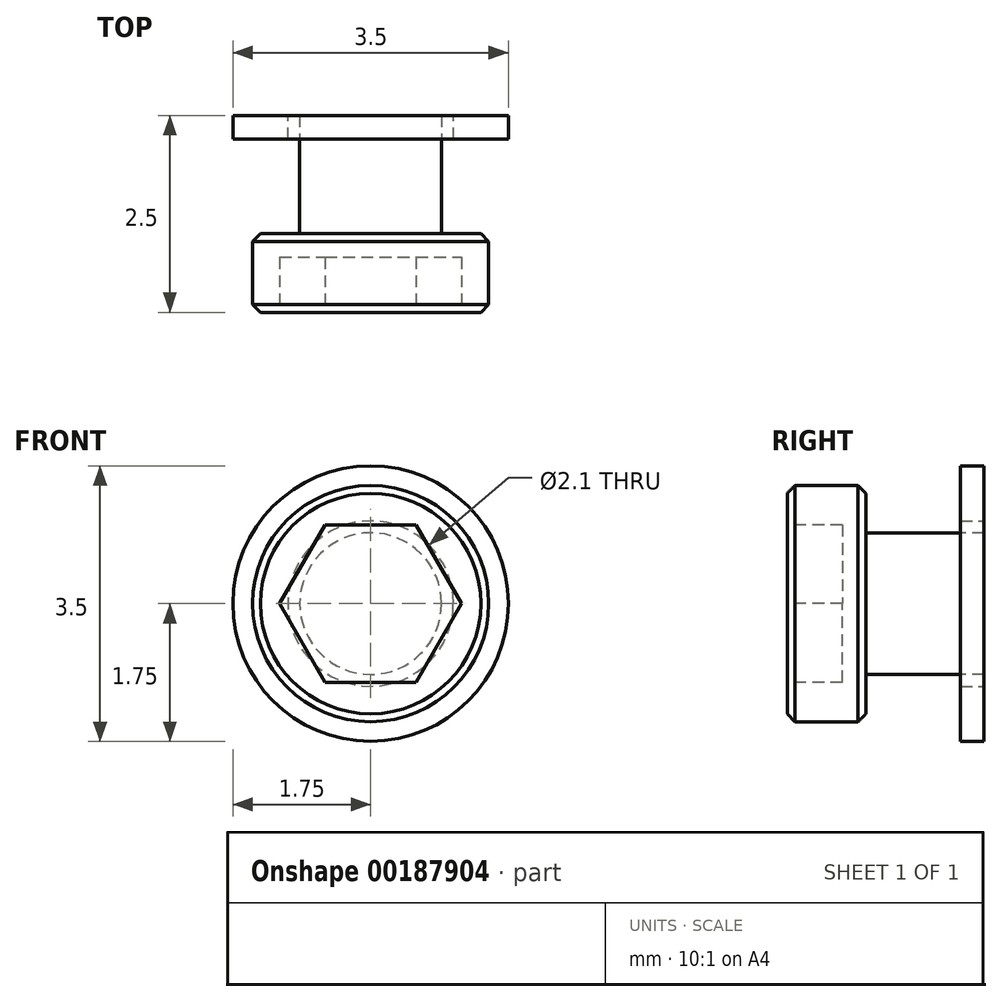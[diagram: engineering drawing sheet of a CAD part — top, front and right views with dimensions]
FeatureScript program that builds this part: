
annotation { "Feature Type Name" : "Feature", "Feature Type Description" : "" }
export const myFeature = defineFeature(function(context is Context, id is Id, definition is map)
    precondition{}
    {
        {
            var Q0;
            Q0=qCreatedBy(makeId("Front.planeOp"),FACE);
            var sketch = newSketch(context, id + "F0", { "sketchPlane" : qUnion([Q0])});
            skCircle(sketch, "E0", {"center": v(0, 0) * mm, "radius": 1.05 * mm});
            skCircle(sketch, "E1", {"center": v(0, 0) * mm, "radius": 1.75 * mm});
            skSolve(sketch);
        }
        {
            var Q0;
            Q0 = qSketchRegion(id + "F0", true);
            extrude(context, id + "F1", {"entities" : qUnion([Q0]), "depth" : 0.3 * mm});
        }
        {
            var Q0;
            Q0=qCreatedBy(makeId("Right.planeOp"),FACE);
            var sketch = newSketch(context, id + "F2", { "sketchPlane" : qUnion([Q0])});
            skLineSegment(sketch, "E2", {"start": v(-5.03, 0) * mm, "end": v(3.17, 0) * mm, "construction": true});
            skLineSegment(sketch, "E3", {"start": v(0, 0) * mm, "end": v(0, -0.9) * mm});
            skLineSegment(sketch, "E4", {"start": v(0, -0.9) * mm, "end": v(-1.5, -0.9) * mm});
            skLineSegment(sketch, "E5", {"start": v(-1.5, -0.9) * mm, "end": v(-1.5, -1.5) * mm});
            skLineSegment(sketch, "E6", {"start": v(-1.5, -1.5) * mm, "end": v(-2.5, -1.5) * mm});
            skLineSegment(sketch, "E7", {"start": v(-2.5, -1.5) * mm, "end": v(-2.5, 0) * mm});
            skLineSegment(sketch, "E8", {"start": v(-2.5, 0) * mm, "end": v(0, 0) * mm});
            skSolve(sketch);
        }
        {
            var Q0;
            Q0 = qSketchRegion(id + "F2", true);
            var Q1;
            Q1=sQuery(id+"F2.wireOp",EDGE,"E2");
            revolve(context, id + "F3", {"entities" : qUnion([Q0]), "axis" : qUnion([Q1]), "revolveType" : RevolveType.FULL});
        }
        {
            var Q0;
            Q0=makeQuery(id+"F3.opRevolve","SWEPT_FACE",FACE,{"disambiguationData":[OSD([sQuery(id+"F2.wireOp",EDGE,"E7")])]});
            var sketch = newSketch(context, id + "F4", { "sketchPlane" : qUnion([Q0])});
            skCircle(sketch, "E9.cCircle", {"center": v(0, 0) * mm, "radius": 1 * mm, "construction": true});
            skLineSegment(sketch, "E9.0", {"start": v(0.58, 1) * mm, "end": v(1.15, 0) * mm});
            skLineSegment(sketch, "E9.1", {"start": v(1.15, 0) * mm, "end": v(0.58, -1) * mm});
            skLineSegment(sketch, "E9.2", {"start": v(0.58, -1) * mm, "end": v(-0.58, -1) * mm});
            skLineSegment(sketch, "E9.3", {"start": v(-0.58, -1) * mm, "end": v(-1.15, 0) * mm});
            skLineSegment(sketch, "E9.4", {"start": v(-1.15, 0) * mm, "end": v(-0.58, 1) * mm});
            skLineSegment(sketch, "E9.5", {"start": v(-0.58, 1) * mm, "end": v(0.58, 1) * mm});
            skPoint(sketch, "E9.0.midPoint", {"position": v(0.87, 0.5) * mm});
            skSolve(sketch);
        }
        {
            var Q0;
            Q0 = qSketchRegion(id + "F4", true);
            extrude(context, id + "F5", {"entities" : qUnion([Q0]), "operationType" : NewBodyOperationType.REMOVE, "oppositeDirection" : true, "depth" : 0.7 * mm});
        }
        {
            var Q0;
            Q0=makeQuery(id+"F3.opRevolve","SWEPT_EDGE",EDGE,{"disambiguationData":[OSD([sQuery(id+"F2.wireOp",EDGE,"E6"),sQuery(id+"F2.wireOp",EDGE,"E7")])]});
            var Q1;
            Q1=makeQuery(id+"F3.opRevolve","SWEPT_EDGE",EDGE,{"disambiguationData":[OSD([sQuery(id+"F2.wireOp",EDGE,"E5"),sQuery(id+"F2.wireOp",EDGE,"E6")])]});
            chamfer(context, id + "F6", {"entities" : qUnion([Q0, Q1]), "width" : 0.1 * mm, "tangentPropagation" : true});
        }
    });
